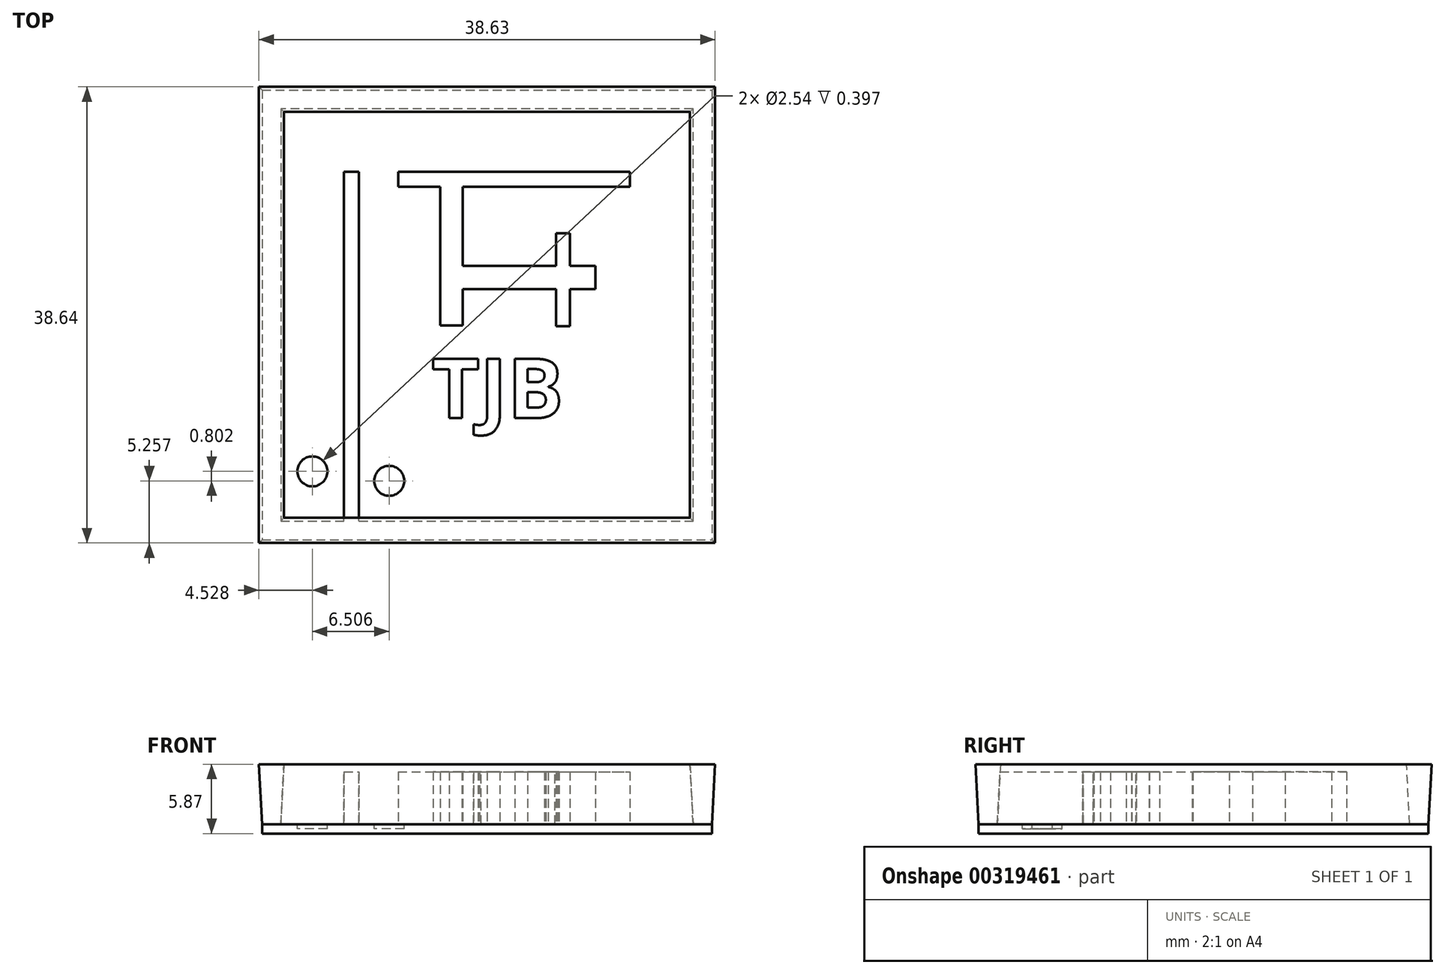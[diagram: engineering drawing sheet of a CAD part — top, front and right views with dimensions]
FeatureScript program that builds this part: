
annotation { "Feature Type Name" : "Feature", "Feature Type Description" : "" }
export const myFeature = defineFeature(function(context is Context, id is Id, definition is map)
    precondition{}
    {
        {
            var Q0;
            Q0=qCreatedBy(makeId("Top.planeOp"),FACE);
            var sketch = newSketch(context, id + "F0", { "sketchPlane" : qUnion([Q0])});
            skLineSegment(sketch, "E0.bottom", {"start": v(-22.9, 18.33) * mm, "end": v(15.2, 18.33) * mm});
            skLineSegment(sketch, "E0.top", {"start": v(-22.9, -19.77) * mm, "end": v(15.2, -19.77) * mm});
            skLineSegment(sketch, "E0.left", {"start": v(-22.9, 18.33) * mm, "end": v(-22.9, -19.77) * mm});
            skLineSegment(sketch, "E0.right", {"start": v(15.2, 18.33) * mm, "end": v(15.2, -19.77) * mm});
            skLineSegment(sketch, "E1.bottom", {"start": v(30.18, 17.75) * mm, "end": v(68.28, 17.75) * mm});
            skLineSegment(sketch, "E1.top", {"start": v(30.18, -20.35) * mm, "end": v(68.28, -20.35) * mm});
            skLineSegment(sketch, "E1.left", {"start": v(30.18, 17.75) * mm, "end": v(30.18, -20.35) * mm});
            skLineSegment(sketch, "E1.right", {"start": v(68.28, 17.75) * mm, "end": v(68.28, -20.35) * mm});
            skSolve(sketch);
        }
        {
            var Q0;
            Q0=makeQuery(id+"F0.imprint","IMPRINT",FACE,{"disambiguationData":[TD([[makeQuery(id+"F0.imprint","IMPRINT",EDGE,{"derivedFrom":sQuery(id+"F0.wireOp",EDGE,"E0.bottom")}),-1.0]])]});
            extrude(context, id + "F1", {"entities" : qUnion([Q0]), "depth" : 0.8 * mm, "offsetDistance" : 25.4 * mm});
        }
        {
            var Q0;
            Q0=makeQuery(id+"F1.opExtrude","CAP_FACE",FACE,{"disambiguationData":[OSD([sQuery(id+"F0.wireOp",EDGE,"E0.bottom"),sQuery(id+"F0.wireOp",EDGE,"E0.top"),sQuery(id+"F0.wireOp",EDGE,"E0.left"),sQuery(id+"F0.wireOp",EDGE,"E0.right")])],"isStart":false});
            var sketch = newSketch(context, id + "F2", { "sketchPlane" : qUnion([Q0])});
            skLineSegment(sketch, "E2.0", {"start": v(-21.3, 16.74) * mm, "end": v(13.62, 16.74) * mm});
            skLineSegment(sketch, "E2.1", {"start": v(-21.3, 16.74) * mm, "end": v(-21.3, -18.18) * mm});
            skLineSegment(sketch, "E2.2", {"start": v(-21.3, -18.18) * mm, "end": v(13.62, -18.18) * mm});
            skLineSegment(sketch, "E2.3", {"start": v(13.62, 16.74) * mm, "end": v(13.62, -18.18) * mm});
            skSolve(sketch);
        }
        {
            var Q0;
            Q0=makeQuery(id+"F2.imprint","IMPRINT",FACE,{"disambiguationData":[TD([[makeQuery(id+"F2.imprint","IMPRINT",EDGE,{"derivedFrom":sQuery(id+"F2.wireOp",EDGE,"E2.0")}),1.0]])]});
            extrude(context, id + "F3", {"entities" : qUnion([Q0]), "operationType" : NewBodyOperationType.ADD, "depth" : 5.08 * mm, "hasDraft" : true, "draftAngle" : 3 * degree, "offsetDistance" : 25.4 * mm});
        }
        {
            var Q0;
            Q0=makeQuery(id+"F1.opExtrude","CAP_FACE",FACE,{"disambiguationData":[OSD([sQuery(id+"F0.wireOp",EDGE,"E0.bottom"),sQuery(id+"F0.wireOp",EDGE,"E0.top"),sQuery(id+"F0.wireOp",EDGE,"E0.left"),sQuery(id+"F0.wireOp",EDGE,"E0.right")])],"isStart":false});
            var sketch = newSketch(context, id + "F4", { "sketchPlane" : qUnion([Q0])});
            skLineSegment(sketch, "E3.bottom", {"start": v(-15.96, -18.18) * mm, "end": v(-14.69, -18.18) * mm});
            skLineSegment(sketch, "E3.top", {"start": v(-15.96, 11.4) * mm, "end": v(-14.69, 11.4) * mm});
            skLineSegment(sketch, "E3.left", {"start": v(-15.96, -18.18) * mm, "end": v(-15.96, 11.4) * mm});
            skLineSegment(sketch, "E3.right", {"start": v(-14.69, -18.18) * mm, "end": v(-14.69, 11.4) * mm});
            skLineSegment(sketch, "E4.bottom", {"start": v(-11.37, 11.4) * mm, "end": v(8.27, 11.4) * mm});
            skLineSegment(sketch, "E4.top", {"start": v(-11.37, 10.13) * mm, "end": v(-7.82, 10.13) * mm});
            skLineSegment(sketch, "E4.left", {"start": v(-11.37, 11.4) * mm, "end": v(-11.37, 10.13) * mm});
            skLineSegment(sketch, "E4.right", {"start": v(8.27, 11.4) * mm, "end": v(8.27, 10.13) * mm});
            skLineSegment(sketch, "E5.top", {"start": v(-7.82, -1.61) * mm, "end": v(-5.9, -1.61) * mm});
            skLineSegment(sketch, "E5.left", {"start": v(-7.82, 10.13) * mm, "end": v(-7.82, -1.61) * mm});
            skLineSegment(sketch, "E5.right", {"start": v(-5.9, 10.13) * mm, "end": v(-5.9, 3.43) * mm});
            skLineSegment(sketch, "E6.bottom", {"start": v(-5.9, 3.43) * mm, "end": v(2, 3.43) * mm});
            skLineSegment(sketch, "E6.top", {"start": v(-5.9, 1.47) * mm, "end": v(2, 1.47) * mm});
            skLineSegment(sketch, "E6.right", {"start": v(5.36, 3.43) * mm, "end": v(5.36, 1.47) * mm});
            skLineSegment(sketch, "E7.trimOffspring", {"start": v(-5.9, 10.13) * mm, "end": v(8.27, 10.13) * mm});
            skLineSegment(sketch, "E8.trimOffspring", {"start": v(-5.9, 1.47) * mm, "end": v(-5.9, -1.61) * mm});
            skLineSegment(sketch, "E9", {"start": v(-21.3, -18.18) * mm, "end": v(-15.96, -18.18) * mm});
            skCircle(sketch, "E10", {"center": v(-18.63, -13.98) * mm, "radius": 1.27 * mm});
            skPoint(sketch, "E10.centerSnap0", {"position": v(-18.63, -18.18) * mm});
            skCircle(sketch, "E11", {"center": v(-12.13, -14.78) * mm, "radius": 1.27 * mm});
            skText(sketch, "E12", { "text": "TJB", "fontName": "OpenSans-Bold.ttf"});
            skLineSegment(sketch, "E13", {"start": v(2.03, 7.34) * mm, "end": v(8.25, 7.34) * mm});
            skLineSegment(sketch, "E14.bottom", {"start": v(8.88, 4.9) * mm, "end": v(10.24, 4.9) * mm});
            skLineSegment(sketch, "E14.top", {"start": v(8.88, -3.94) * mm, "end": v(8.92, -3.94) * mm});
            skLineSegment(sketch, "E14.left", {"start": v(8.88, 4.9) * mm, "end": v(8.88, -3.94) * mm});
            skLineSegment(sketch, "E14.right", {"start": v(10.24, 4.9) * mm, "end": v(10.24, -3.94) * mm});
            skLineSegment(sketch, "E15.bottom", {"start": v(2, -1.68) * mm, "end": v(3.2, -1.68) * mm});
            skLineSegment(sketch, "E15.top", {"start": v(2, 6.19) * mm, "end": v(3.2, 6.19) * mm});
            skLineSegment(sketch, "E15.left", {"start": v(2, -1.68) * mm, "end": v(2, 1.47) * mm});
            skLineSegment(sketch, "E15.right", {"start": v(3.2, -1.68) * mm, "end": v(3.2, 1.47) * mm});
            skLineSegment(sketch, "E16.bottom", {"start": v(10.24, -3.94) * mm, "end": v(8.92, -3.94) * mm});
            skLineSegment(sketch, "E16.top", {"start": v(10.24, -16.76) * mm, "end": v(8.92, -16.76) * mm});
            skLineSegment(sketch, "E16.left", {"start": v(10.24, -3.94) * mm, "end": v(10.24, -8.18) * mm});
            skLineSegment(sketch, "E16.right", {"start": v(8.92, -3.94) * mm, "end": v(8.92, -8.18) * mm});
            skLineSegment(sketch, "E17.bottom", {"start": v(5.05, -8.18) * mm, "end": v(8.92, -8.18) * mm});
            skLineSegment(sketch, "E17.top", {"start": v(5.05, -9.43) * mm, "end": v(8.92, -9.43) * mm});
            skLineSegment(sketch, "E17.left", {"start": v(5.05, -8.18) * mm, "end": v(5.05, -9.43) * mm});
            skLineSegment(sketch, "E17.right", {"start": v(12.44, -8.18) * mm, "end": v(12.44, -9.43) * mm});
            skLineSegment(sketch, "E18.trimOffspring", {"start": v(10.24, -8.18) * mm, "end": v(12.44, -8.18) * mm});
            skLineSegment(sketch, "E19.trimOffspring", {"start": v(10.24, -9.43) * mm, "end": v(10.24, -16.76) * mm});
            skLineSegment(sketch, "E20.trimOffspring", {"start": v(10.24, -9.43) * mm, "end": v(12.44, -9.43) * mm});
            skLineSegment(sketch, "E21.trimOffspring", {"start": v(8.92, -9.43) * mm, "end": v(8.92, -16.76) * mm});
            skLineSegment(sketch, "E22.trimOffspring", {"start": v(3.2, 1.47) * mm, "end": v(5.36, 1.47) * mm});
            skLineSegment(sketch, "E23.trimOffspring", {"start": v(2, 3.43) * mm, "end": v(2, 6.19) * mm});
            skLineSegment(sketch, "E24.trimOffspring", {"start": v(3.2, 3.43) * mm, "end": v(5.36, 3.43) * mm});
            skLineSegment(sketch, "E25.trimOffspring", {"start": v(3.2, 3.43) * mm, "end": v(3.2, 6.19) * mm});
            skText(sketch, "E26", { "text": "tjb", "fontName": "OpenSans-Regular.ttf"});
            const initialGuessF4  = {"E12": [-0.00854, -0.00947, 1, 0, 0.00508], "E26": [-0.00166, -0.0165, 1, 0, 0.00508]};
            skSetInitialGuess(sketch, initialGuessF4);
            skSolve(sketch);
        }
        {
            var Q0;
            Q0=makeQuery(id+"F4.imprint","IMPRINT",FACE,{"disambiguationData":[TD([[makeQuery(id+"F4.imprint","IMPRINT",EDGE,{"derivedFrom":sQuery(id+"F4.wireOp",EDGE,"E10")}),1.0]])]});
            var Q1;
            Q1=makeQuery(id+"F4.imprint","IMPRINT",FACE,{"disambiguationData":[TD([[makeQuery(id+"F4.imprint","IMPRINT",EDGE,{"derivedFrom":sQuery(id+"F4.wireOp",EDGE,"E11")}),1.0]])]});
            extrude(context, id + "F5", {"entities" : qUnion([Q0, Q1]), "operationType" : NewBodyOperationType.REMOVE, "oppositeDirection" : true, "depth" : 0.4 * mm});
        }
        {
            var Q0;
            Q0=makeQuery(id+"F4.imprint","IMPRINT",FACE,{"disambiguationData":[TD([[makeQuery(id+"F4.imprint","IMPRINT",EDGE,{"derivedFrom":sQuery(id+"F4.wireOp",EDGE,"E3.bottom")}),1.0]])]});
            var Q1;
            Q1=makeQuery(id+"F4.imprint","IMPRINT",FACE,{"disambiguationData":[TD([[makeQuery(id+"F4.imprint","IMPRINT",EDGE,{"derivedFrom":sQuery(id+"F4.wireOp",EDGE,"E4.bottom")}),-1.0]])]});
            extrude(context, id + "F6", {"entities" : qUnion([Q0, Q1]), "operationType" : NewBodyOperationType.ADD, "depth" : 4.44 * mm});
        }
        {
            var Q0;
            Q0=makeQuery(id+"F4.imprint","IMPRINT",FACE,{"disambiguationData":[TD([[makeQuery(id+"F4.imprint","IMPRINT",EDGE,{"derivedFrom":sQuery(id+"F4.wireOp",EDGE,"E12.sketch_text.stroke-0")}),-1.0]])]});
            var Q1;
            Q1=makeQuery(id+"F4.imprint","IMPRINT",FACE,{"disambiguationData":[TD([[makeQuery(id+"F4.imprint","IMPRINT",EDGE,{"derivedFrom":sQuery(id+"F4.wireOp",EDGE,"E12.sketch_text.stroke-8")}),-1.0]])]});
            var Q2;
            Q2=makeQuery(id+"F4.imprint","IMPRINT",FACE,{"disambiguationData":[TD([[makeQuery(id+"F4.imprint","IMPRINT",EDGE,{"derivedFrom":sQuery(id+"F4.wireOp",EDGE,"E12.sketch_text.stroke-18")}),-1.0]])]});
            extrude(context, id + "F7", {"entities" : qUnion([Q0, Q1, Q2]), "operationType" : NewBodyOperationType.ADD, "depth" : 4.44 * mm});
        }
    });
